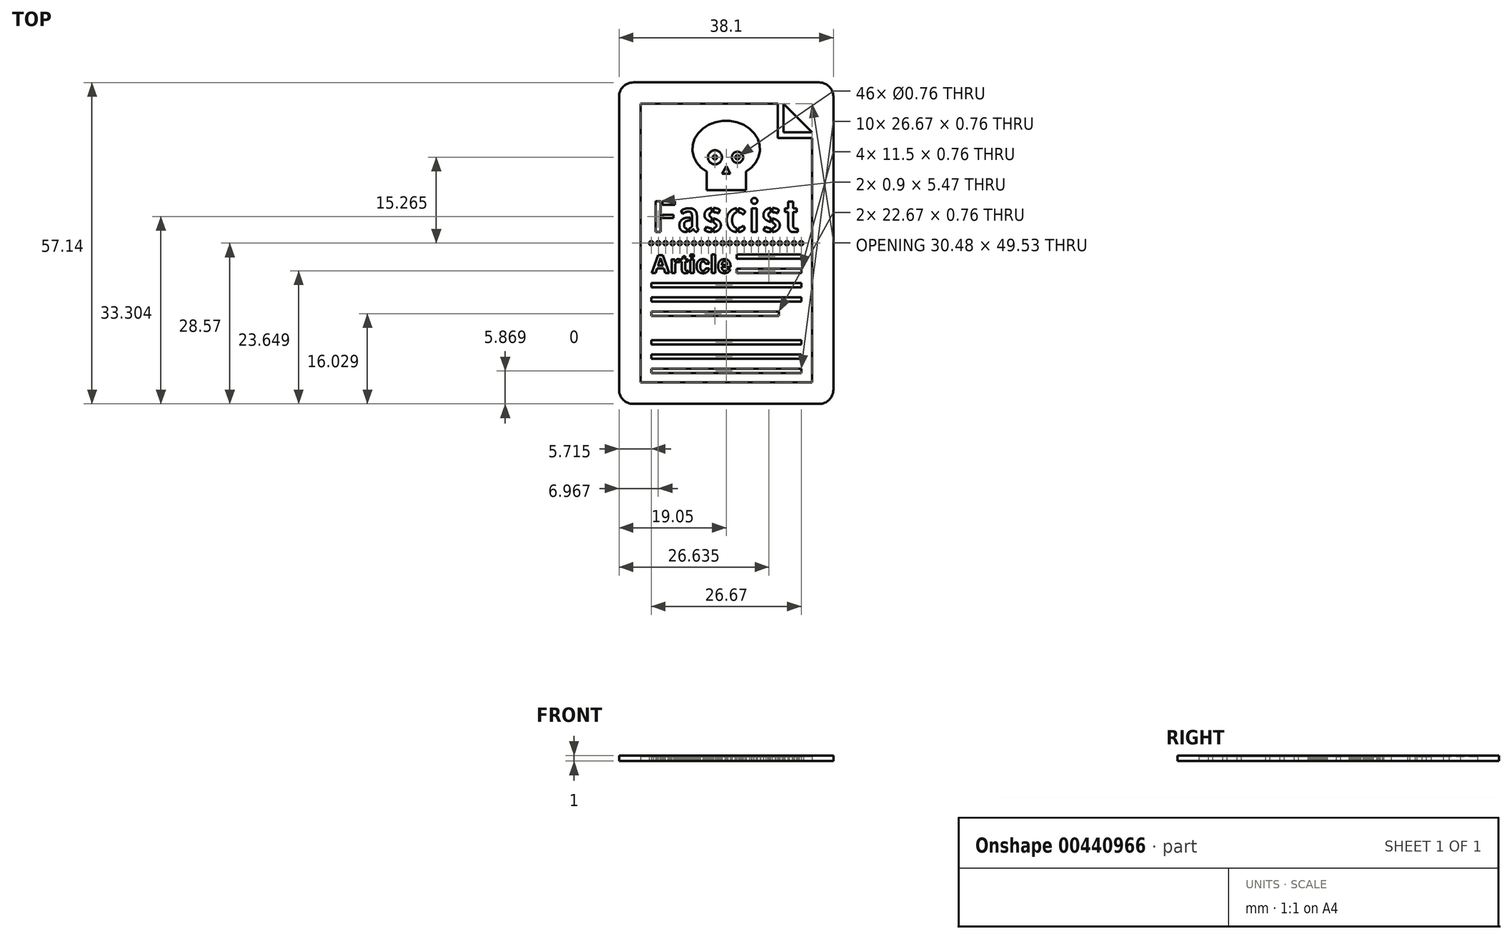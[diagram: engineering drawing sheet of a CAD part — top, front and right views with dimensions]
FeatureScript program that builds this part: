
annotation { "Feature Type Name" : "Feature", "Feature Type Description" : "" }
export const myFeature = defineFeature(function(context is Context, id is Id, definition is map)
    precondition{}
    {
        {
            var Q0;
            Q0=qCreatedBy(makeId("Top.planeOp"),FACE);
            var sketch = newSketch(context, id + "F0", { "sketchPlane" : qUnion([Q0])});
            skLineSegment(sketch, "E0.bottom", {"start": v(16.5, 28.58) * mm, "end": v(-16.51, 28.58) * mm});
            skLineSegment(sketch, "E0.top", {"start": v(16.51, -28.58) * mm, "end": v(-16.5, -28.58) * mm});
            skLineSegment(sketch, "E0.left", {"start": v(19.05, 26.04) * mm, "end": v(19.05, -26.04) * mm});
            skLineSegment(sketch, "E0.right", {"start": v(-19.05, 26.04) * mm, "end": v(-19.05, -26.04) * mm});
            skPoint(sketch, "E0.middle", {"position": v(0, 0) * mm});
            skPoint(sketch, "E1.visualSharp", {"position": v(-19.05, 28.58) * mm});
            skArc(sketch, "E1.filletArc", {"start": v(-16.51, 28.58) * mm, "mid": v(-18.3, 27.83) * mm, "end": v(-19.05, 26.04) * mm});
            skPoint(sketch, "E2.visualSharp", {"position": v(19.05, 28.58) * mm});
            skArc(sketch, "E2.filletArc", {"start": v(19.05, 26.04) * mm, "mid": v(18.3, 27.83) * mm, "end": v(16.5, 28.58) * mm});
            skPoint(sketch, "E3.visualSharp", {"position": v(19.05, -28.58) * mm});
            skArc(sketch, "E3.filletArc", {"start": v(16.51, -28.58) * mm, "mid": v(18.3, -27.83) * mm, "end": v(19.05, -26.04) * mm});
            skPoint(sketch, "E4.visualSharp", {"position": v(-19.05, -28.58) * mm});
            skArc(sketch, "E4.filletArc", {"start": v(-19.05, -26.04) * mm, "mid": v(-18.3, -27.83) * mm, "end": v(-16.5, -28.58) * mm});
            skLineSegment(sketch, "E5.bottom", {"start": v(9.14, 24.76) * mm, "end": v(-15.24, 24.76) * mm});
            skLineSegment(sketch, "E5.top", {"start": v(15.24, -24.77) * mm, "end": v(-15.24, -24.77) * mm});
            skLineSegment(sketch, "E5.left", {"start": v(15.24, 18.67) * mm, "end": v(15.24, -24.77) * mm});
            skLineSegment(sketch, "E5.right", {"start": v(-15.24, 24.77) * mm, "end": v(-15.24, -24.77) * mm});
            skLineSegment(sketch, "E6.top", {"start": v(15.24, 19.68) * mm, "end": v(10.16, 19.68) * mm});
            skLineSegment(sketch, "E6.right", {"start": v(10.16, 24.76) * mm, "end": v(10.16, 19.68) * mm});
            skLineSegment(sketch, "E7", {"start": v(10.16, 24.76) * mm, "end": v(15.24, 19.68) * mm});
            skPoint(sketch, "E8.orphan", {"position": v(15.24, 24.76) * mm});
            skLineSegment(sketch, "E9.0", {"start": v(15.24, 18.67) * mm, "end": v(9.14, 18.67) * mm});
            skLineSegment(sketch, "E9.1", {"start": v(9.14, 24.76) * mm, "end": v(9.14, 18.67) * mm});
            skEllipticalArc(sketch, "E10", {});
            skLineSegment(sketch, "E11.bottom", {"start": v(3.5, 9.4) * mm, "end": v(-3.5, 9.4) * mm});
            skLineSegment(sketch, "E11.left", {"start": v(3.5, 9.4) * mm, "end": v(3.5, 12.7) * mm});
            skLineSegment(sketch, "E11.right", {"start": v(-3.5, 9.4) * mm, "end": v(-3.5, 12.7) * mm});
            skPoint(sketch, "E11.middle", {"position": v(0, 15.06) * mm});
            skPoint(sketch, "E11.top.start.orphan", {"position": v(3.5, 20.72) * mm});
            skPoint(sketch, "E12.orphan", {"position": v(-3.5, 20.72) * mm});
            skCircle(sketch, "E13", {"center": v(-2, 15.26) * mm, "radius": 1.25 * mm});
            skLineSegment(sketch, "E14", {"start": v(0, 13.66) * mm, "end": v(-0.75, 12.37) * mm});
            skLineSegment(sketch, "E15", {"start": v(-0.75, 12.37) * mm, "end": v(0.75, 12.37) * mm});
            skLineSegment(sketch, "E16", {"start": v(0, 13.66) * mm, "end": v(0.75, 12.37) * mm});
            skCircle(sketch, "E17", {"center": v(2, 15.26) * mm, "radius": 1 * mm});
            skLineSegment(sketch, "E18.0", {"start": v(2.74, 10.17) * mm, "end": v(2.13, 10.17) * mm});
            skLineSegment(sketch, "E18.1", {"start": v(2.74, 10.17) * mm, "end": v(2.74, 13.15) * mm});
            skFitSpline(sketch, "E18.2", {"points": [v(5.17, 15.96) * mm, v(5.27, 16.76) * mm, v(5.17, 17.57) * mm, v(4.9, 18.34) * mm, v(4.42, 19.08) * mm, v(3.78, 19.73) * mm, v(2.99, 20.28) * mm, v(2.06, 20.7) * mm, v(1.06, 20.94) * mm, v(0, 21.03) * mm, v(-1.06, 20.94) * mm, v(-2.06, 20.7) * mm, v(-2.99, 20.28) * mm, v(-3.78, 19.73) * mm, v(-4.42, 19.08) * mm, v(-4.9, 18.34) * mm, v(-5.17, 17.57) * mm, v(-5.27, 16.76) * mm, v(-5.17, 15.96) * mm, v(-4.9, 15.19) * mm, v(-4.42, 14.45) * mm, v(-3.78, 13.8) * mm, v(-2.99, 13.25) * mm, v(-2.06, 12.84) * mm, v(-1.06, 12.59) * mm, v(0, 12.5) * mm, v(1.06, 12.59) * mm, v(2.06, 12.84) * mm, v(2.99, 13.25) * mm, v(3.78, 13.8) * mm, v(4.42, 14.45) * mm, v(4.9, 15.19) * mm, v(5.17, 15.96) * mm, v(5.27, 16.76) * mm, v(5.17, 17.57) * mm]});
            skLineSegment(sketch, "E18.3", {"start": v(-2.74, 10.17) * mm, "end": v(-2.74, 13.15) * mm});
            skLineSegment(sketch, "E19.top", {"start": v(-2.13, 11.17) * mm, "end": v(-1.78, 11.17) * mm});
            skLineSegment(sketch, "E19.left", {"start": v(-2.13, 10.17) * mm, "end": v(-2.13, 11.17) * mm});
            skLineSegment(sketch, "E19.right", {"start": v(-1.78, 10.17) * mm, "end": v(-1.78, 11.17) * mm});
            skLineSegment(sketch, "E20.trimOffspring", {"start": v(-2.13, 10.17) * mm, "end": v(-2.74, 10.17) * mm});
            skLineSegment(sketch, "E21.top", {"start": v(-0.83, 11.17) * mm, "end": v(-0.48, 11.17) * mm});
            skLineSegment(sketch, "E21.left", {"start": v(-0.83, 10.17) * mm, "end": v(-0.83, 11.17) * mm});
            skLineSegment(sketch, "E21.right", {"start": v(-0.48, 10.17) * mm, "end": v(-0.48, 11.17) * mm});
            skLineSegment(sketch, "E22.top", {"start": v(0.48, 11.17) * mm, "end": v(0.83, 11.17) * mm});
            skLineSegment(sketch, "E22.left", {"start": v(0.48, 10.17) * mm, "end": v(0.48, 11.17) * mm});
            skLineSegment(sketch, "E22.right", {"start": v(0.83, 10.17) * mm, "end": v(0.83, 11.17) * mm});
            skLineSegment(sketch, "E23.top", {"start": v(1.78, 11.17) * mm, "end": v(2.13, 11.17) * mm});
            skLineSegment(sketch, "E23.left", {"start": v(1.78, 10.17) * mm, "end": v(1.78, 11.17) * mm});
            skLineSegment(sketch, "E23.right", {"start": v(2.13, 10.17) * mm, "end": v(2.13, 11.17) * mm});
            skLineSegment(sketch, "E24.trimOffspring", {"start": v(-0.83, 10.17) * mm, "end": v(-1.78, 10.17) * mm});
            skLineSegment(sketch, "E25.trimOffspring", {"start": v(0.48, 10.17) * mm, "end": v(-0.48, 10.17) * mm});
            skLineSegment(sketch, "E26.trimOffspring", {"start": v(1.78, 10.17) * mm, "end": v(0.83, 10.17) * mm});
            skText(sketch, "E27", { "text": "Fascist", "fontName": "AllertaStencil-Regular.ttf"});
            skCircle(sketch, "E28", {"center": v(-13.34, 0) * mm, "radius": 0.38 * mm});
            skPoint(sketch, "E28.centerSnap0", {"position": v(-15.24, 0) * mm});
            skCircle(sketch, "E29.1.0.0", {"center": v(-12.07, 0) * mm, "radius": 0.38 * mm});
            skCircle(sketch, "E29.2.0.0", {"center": v(-10.8, 0) * mm, "radius": 0.38 * mm});
            skCircle(sketch, "E29.3.0.0", {"center": v(-9.53, 0) * mm, "radius": 0.38 * mm});
            skCircle(sketch, "E29.4.0.0", {"center": v(-8.26, 0) * mm, "radius": 0.38 * mm});
            skCircle(sketch, "E29.5.0.0", {"center": v(-6.99, 0) * mm, "radius": 0.38 * mm});
            skCircle(sketch, "E29.6.0.0", {"center": v(-5.72, 0) * mm, "radius": 0.38 * mm});
            skCircle(sketch, "E29.7.0.0", {"center": v(-4.45, 0) * mm, "radius": 0.38 * mm});
            skCircle(sketch, "E29.8.0.0", {"center": v(-3.18, 0) * mm, "radius": 0.38 * mm});
            skCircle(sketch, "E29.9.0.0", {"center": v(-1.9, 0) * mm, "radius": 0.38 * mm});
            skCircle(sketch, "E29.10.0.0", {"center": v(-0.64, 0) * mm, "radius": 0.38 * mm});
            skCircle(sketch, "E29.11.0.0", {"center": v(0.63, 0) * mm, "radius": 0.38 * mm});
            skCircle(sketch, "E29.12.0.0", {"center": v(1.9, 0) * mm, "radius": 0.38 * mm});
            skCircle(sketch, "E29.13.0.0", {"center": v(3.17, 0) * mm, "radius": 0.38 * mm});
            skCircle(sketch, "E29.14.0.0", {"center": v(4.44, 0) * mm, "radius": 0.38 * mm});
            skCircle(sketch, "E29.15.0.0", {"center": v(5.71, 0) * mm, "radius": 0.38 * mm});
            skCircle(sketch, "E29.16.0.0", {"center": v(6.99, 0) * mm, "radius": 0.38 * mm});
            skCircle(sketch, "E29.17.0.0", {"center": v(8.26, 0) * mm, "radius": 0.38 * mm});
            skCircle(sketch, "E29.18.0.0", {"center": v(9.53, 0) * mm, "radius": 0.38 * mm});
            skCircle(sketch, "E29.19.0.0", {"center": v(10.8, 0) * mm, "radius": 0.38 * mm});
            skCircle(sketch, "E29.20.0.0", {"center": v(12.07, 0) * mm, "radius": 0.38 * mm});
            skCircle(sketch, "E29.21.0.0", {"center": v(13.34, 0) * mm, "radius": 0.38 * mm});
            skLineSegment(sketch, "E29.direction1", {"start": v(-13.34, 0) * mm, "end": v(-12.07, 0) * mm, "construction": true});
            skText(sketch, "E30", { "text": "Article", "fontName": "Arimo-Bold.ttf"});
            skLineSegment(sketch, "E31.bottom", {"start": v(1.84, -2) * mm, "end": v(13.34, -2) * mm});
            skLineSegment(sketch, "E31.top", {"start": v(1.84, -2.76) * mm, "end": v(13.34, -2.76) * mm});
            skLineSegment(sketch, "E31.left", {"start": v(1.84, -2) * mm, "end": v(1.84, -2.76) * mm});
            skLineSegment(sketch, "E31.right", {"start": v(13.34, -2) * mm, "end": v(13.34, -2.76) * mm});
            skLineSegment(sketch, "E32.bottom", {"start": v(1.84, -4.54) * mm, "end": v(13.34, -4.54) * mm});
            skLineSegment(sketch, "E32.top", {"start": v(1.84, -5.3) * mm, "end": v(13.34, -5.3) * mm});
            skLineSegment(sketch, "E32.left", {"start": v(1.84, -4.54) * mm, "end": v(1.84, -5.3) * mm});
            skLineSegment(sketch, "E32.right", {"start": v(13.34, -4.54) * mm, "end": v(13.34, -5.3) * mm});
            skLineSegment(sketch, "E33.bottom", {"start": v(-13.34, -7.08) * mm, "end": v(13.34, -7.08) * mm});
            skLineSegment(sketch, "E33.top", {"start": v(-13.34, -7.84) * mm, "end": v(13.34, -7.84) * mm});
            skLineSegment(sketch, "E33.left", {"start": v(-13.34, -7.08) * mm, "end": v(-13.34, -7.84) * mm});
            skLineSegment(sketch, "E33.right", {"start": v(13.34, -7.08) * mm, "end": v(13.34, -7.84) * mm});
            skLineSegment(sketch, "E34.bottom", {"start": v(-13.34, -9.62) * mm, "end": v(13.34, -9.62) * mm});
            skLineSegment(sketch, "E34.top", {"start": v(-13.34, -10.38) * mm, "end": v(13.34, -10.38) * mm});
            skLineSegment(sketch, "E34.left", {"start": v(-13.34, -9.62) * mm, "end": v(-13.34, -10.38) * mm});
            skLineSegment(sketch, "E34.right", {"start": v(13.34, -9.62) * mm, "end": v(13.34, -10.38) * mm});
            skLineSegment(sketch, "E35.bottom", {"start": v(-13.34, -12.16) * mm, "end": v(9.33, -12.16) * mm});
            skLineSegment(sketch, "E35.top", {"start": v(-13.34, -12.92) * mm, "end": v(9.33, -12.92) * mm});
            skLineSegment(sketch, "E35.left", {"start": v(-13.34, -12.16) * mm, "end": v(-13.34, -12.92) * mm});
            skLineSegment(sketch, "E35.right", {"start": v(9.33, -12.16) * mm, "end": v(9.33, -12.92) * mm});
            skLineSegment(sketch, "E36.bottom", {"start": v(-13.34, -19.78) * mm, "end": v(13.33, -19.78) * mm});
            skLineSegment(sketch, "E36.top", {"start": v(-13.34, -20.54) * mm, "end": v(13.33, -20.54) * mm});
            skLineSegment(sketch, "E36.left", {"start": v(-13.34, -19.78) * mm, "end": v(-13.34, -20.54) * mm});
            skLineSegment(sketch, "E36.right", {"start": v(13.34, -19.78) * mm, "end": v(13.34, -20.54) * mm});
            skLineSegment(sketch, "E37.bottom", {"start": v(-13.34, -22.32) * mm, "end": v(13.34, -22.32) * mm});
            skLineSegment(sketch, "E37.top", {"start": v(-13.34, -23.08) * mm, "end": v(13.34, -23.08) * mm});
            skLineSegment(sketch, "E37.left", {"start": v(-13.34, -22.32) * mm, "end": v(-13.34, -23.08) * mm});
            skLineSegment(sketch, "E37.right", {"start": v(13.34, -22.32) * mm, "end": v(13.34, -23.08) * mm});
            skLineSegment(sketch, "E38.bottom", {"start": v(-13.34, -17.24) * mm, "end": v(13.34, -17.24) * mm});
            skLineSegment(sketch, "E38.top", {"start": v(-13.34, -18) * mm, "end": v(13.34, -18) * mm});
            skLineSegment(sketch, "E38.left", {"start": v(-13.34, -17.24) * mm, "end": v(-13.34, -18) * mm});
            skLineSegment(sketch, "E38.right", {"start": v(13.34, -17.24) * mm, "end": v(13.34, -18) * mm});
            skCircle(sketch, "E39", {"center": v(-2, 15.26) * mm, "radius": 0.38 * mm});
            skCircle(sketch, "E40", {"center": v(2, 15.26) * mm, "radius": 0.38 * mm});
            const initialGuessF0  = {"E10": [0, 0.016765, 1, 0, 0.006, 0.005, 5.335215565796689, 4.089562394972688], "E27": [-0.01324, 0.002, 1, 0, 0.00547], "E30": [-0.01334, -0.0053, 1, 0, 0.0033]};
            skSetInitialGuess(sketch, initialGuessF0);
            skSolve(sketch);
        }
        {
            var Q0;
            Q0 = qSketchRegion(id + "F0", true);
            var Q1;
            Q1=makeQuery(id+"F0.imprint","IMPRINT",FACE,{"disambiguationData":[TD([[makeQuery(id+"F0.imprint","IMPRINT",EDGE,{"derivedFrom":sQuery(id+"F0.wireOp",EDGE,"E10")}),1.0]])]});
            var Q2;
            Q2=makeQuery(id+"F0.imprint","IMPRINT",FACE,{"disambiguationData":[TD([[makeQuery(id+"F0.imprint","IMPRINT",EDGE,{"derivedFrom":sQuery(id+"F0.wireOp",EDGE,"E17")}),1.0]])]});
            var Q3;
            Q3=makeQuery(id+"F0.imprint","IMPRINT",FACE,{"disambiguationData":[TD([[makeQuery(id+"F0.imprint","IMPRINT",EDGE,{"derivedFrom":sQuery(id+"F0.wireOp",EDGE,"E13")}),1.0]])]});
            var Q4;
            Q4=makeQuery(id+"F0.imprint","IMPRINT",FACE,{"disambiguationData":[TD([[makeQuery(id+"F0.imprint","IMPRINT",EDGE,{"derivedFrom":sQuery(id+"F0.wireOp",EDGE,"E14")}),1.0]])]});
            var Q5;
            Q5=makeQuery(id+"F0.imprint","IMPRINT",FACE,{"disambiguationData":[TD([[makeQuery(id+"F0.imprint","IMPRINT",EDGE,{"derivedFrom":sQuery(id+"F0.wireOp",EDGE,"E27.sketch_text.stroke-0")}),-1.0]])]});
            var Q6;
            Q6=makeQuery(id+"F0.imprint","IMPRINT",FACE,{"disambiguationData":[TD([[makeQuery(id+"F0.imprint","IMPRINT",EDGE,{"derivedFrom":sQuery(id+"F0.wireOp",EDGE,"E27.sketch_text.stroke-8")}),-1.0]])]});
            var Q7;
            Q7=makeQuery(id+"F0.imprint","IMPRINT",FACE,{"disambiguationData":[TD([[makeQuery(id+"F0.imprint","IMPRINT",EDGE,{"derivedFrom":sQuery(id+"F0.wireOp",EDGE,"E27.sketch_text.stroke-4")}),-1.0]])]});
            var Q8;
            Q8=makeQuery(id+"F0.imprint","IMPRINT",FACE,{"disambiguationData":[TD([[makeQuery(id+"F0.imprint","IMPRINT",EDGE,{"derivedFrom":sQuery(id+"F0.wireOp",EDGE,"E27.sketch_text.stroke-31")}),-1.0]])]});
            var Q9;
            Q9=makeQuery(id+"F0.imprint","IMPRINT",FACE,{"disambiguationData":[TD([[makeQuery(id+"F0.imprint","IMPRINT",EDGE,{"derivedFrom":sQuery(id+"F0.wireOp",EDGE,"E27.sketch_text.stroke-12")}),-1.0]])]});
            var Q10;
            Q10=makeQuery(id+"F0.imprint","IMPRINT",FACE,{"disambiguationData":[TD([[makeQuery(id+"F0.imprint","IMPRINT",EDGE,{"derivedFrom":sQuery(id+"F0.wireOp",EDGE,"E27.sketch_text.stroke-96")}),-1.0]])]});
            var Q11;
            Q11=makeQuery(id+"F0.imprint","IMPRINT",FACE,{"disambiguationData":[TD([[makeQuery(id+"F0.imprint","IMPRINT",EDGE,{"derivedFrom":sQuery(id+"F0.wireOp",EDGE,"E27.sketch_text.stroke-87")}),-1.0]])]});
            var Q12;
            Q12=makeQuery(id+"F0.imprint","IMPRINT",FACE,{"disambiguationData":[TD([[makeQuery(id+"F0.imprint","IMPRINT",EDGE,{"derivedFrom":sQuery(id+"F0.wireOp",EDGE,"E27.sketch_text.stroke-67")}),-1.0]])]});
            var Q13;
            Q13=makeQuery(id+"F0.imprint","IMPRINT",FACE,{"disambiguationData":[TD([[makeQuery(id+"F0.imprint","IMPRINT",EDGE,{"derivedFrom":sQuery(id+"F0.wireOp",EDGE,"E27.sketch_text.stroke-81")}),-1.0]])]});
            var Q14;
            Q14=makeQuery(id+"F0.imprint","IMPRINT",FACE,{"disambiguationData":[TD([[makeQuery(id+"F0.imprint","IMPRINT",EDGE,{"derivedFrom":sQuery(id+"F0.wireOp",EDGE,"E27.sketch_text.stroke-116")}),-1.0]])]});
            var Q15;
            Q15=makeQuery(id+"F0.imprint","IMPRINT",FACE,{"disambiguationData":[TD([[makeQuery(id+"F0.imprint","IMPRINT",EDGE,{"derivedFrom":sQuery(id+"F0.wireOp",EDGE,"E27.sketch_text.stroke-122")}),-1.0]])]});
            var Q16;
            Q16=makeQuery(id+"F0.imprint","IMPRINT",FACE,{"disambiguationData":[TD([[makeQuery(id+"F0.imprint","IMPRINT",EDGE,{"derivedFrom":sQuery(id+"F0.wireOp",EDGE,"E27.sketch_text.stroke-110")}),-1.0]])]});
            var Q17;
            Q17=makeQuery(id+"F0.imprint","IMPRINT",FACE,{"disambiguationData":[TD([[makeQuery(id+"F0.imprint","IMPRINT",EDGE,{"derivedFrom":sQuery(id+"F0.wireOp",EDGE,"E27.sketch_text.stroke-142")}),-1.0]])]});
            var Q18;
            Q18=makeQuery(id+"F0.imprint","IMPRINT",FACE,{"disambiguationData":[TD([[makeQuery(id+"F0.imprint","IMPRINT",EDGE,{"derivedFrom":sQuery(id+"F0.wireOp",EDGE,"E27.sketch_text.stroke-138")}),-1.0]])]});
            var Q19;
            Q19=makeQuery(id+"F0.imprint","IMPRINT",FACE,{"disambiguationData":[TD([[makeQuery(id+"F0.imprint","IMPRINT",EDGE,{"derivedFrom":sQuery(id+"F0.wireOp",EDGE,"E27.sketch_text.stroke-170")}),-1.0]])]});
            var Q20;
            Q20=makeQuery(id+"F0.imprint","IMPRINT",FACE,{"disambiguationData":[TD([[makeQuery(id+"F0.imprint","IMPRINT",EDGE,{"derivedFrom":sQuery(id+"F0.wireOp",EDGE,"E27.sketch_text.stroke-179")}),-1.0]])]});
            var Q21;
            Q21=makeQuery(id+"F0.imprint","IMPRINT",FACE,{"disambiguationData":[TD([[makeQuery(id+"F0.imprint","IMPRINT",EDGE,{"derivedFrom":sQuery(id+"F0.wireOp",EDGE,"E27.sketch_text.stroke-150")}),-1.0]])]});
            var Q22;
            Q22=makeQuery(id+"F0.imprint","IMPRINT",FACE,{"disambiguationData":[TD([[makeQuery(id+"F0.imprint","IMPRINT",EDGE,{"derivedFrom":sQuery(id+"F0.wireOp",EDGE,"E27.sketch_text.stroke-164")}),-1.0]])]});
            var Q23;
            Q23=makeQuery(id+"F0.imprint","IMPRINT",FACE,{"disambiguationData":[TD([[makeQuery(id+"F0.imprint","IMPRINT",EDGE,{"derivedFrom":sQuery(id+"F0.wireOp",EDGE,"E27.sketch_text.stroke-193")}),-1.0]])]});
            var Q24;
            Q24=makeQuery(id+"F0.imprint","IMPRINT",FACE,{"disambiguationData":[TD([[makeQuery(id+"F0.imprint","IMPRINT",EDGE,{"derivedFrom":sQuery(id+"F0.wireOp",EDGE,"E28")}),1.0]])]});
            var Q25;
            Q25=makeQuery(id+"F0.imprint","IMPRINT",FACE,{"disambiguationData":[TD([[makeQuery(id+"F0.imprint","IMPRINT",EDGE,{"derivedFrom":sQuery(id+"F0.wireOp",EDGE,"E29.1.0.0")}),1.0]])]});
            var Q26;
            Q26=makeQuery(id+"F0.imprint","IMPRINT",FACE,{"disambiguationData":[TD([[makeQuery(id+"F0.imprint","IMPRINT",EDGE,{"derivedFrom":sQuery(id+"F0.wireOp",EDGE,"E29.2.0.0")}),1.0]])]});
            var Q27;
            Q27=makeQuery(id+"F0.imprint","IMPRINT",FACE,{"disambiguationData":[TD([[makeQuery(id+"F0.imprint","IMPRINT",EDGE,{"derivedFrom":sQuery(id+"F0.wireOp",EDGE,"E29.3.0.0")}),1.0]])]});
            var Q28;
            Q28=makeQuery(id+"F0.imprint","IMPRINT",FACE,{"disambiguationData":[TD([[makeQuery(id+"F0.imprint","IMPRINT",EDGE,{"derivedFrom":sQuery(id+"F0.wireOp",EDGE,"E29.4.0.0")}),1.0]])]});
            var Q29;
            Q29=makeQuery(id+"F0.imprint","IMPRINT",FACE,{"disambiguationData":[TD([[makeQuery(id+"F0.imprint","IMPRINT",EDGE,{"derivedFrom":sQuery(id+"F0.wireOp",EDGE,"E29.5.0.0")}),1.0]])]});
            var Q30;
            Q30=makeQuery(id+"F0.imprint","IMPRINT",FACE,{"disambiguationData":[TD([[makeQuery(id+"F0.imprint","IMPRINT",EDGE,{"derivedFrom":sQuery(id+"F0.wireOp",EDGE,"E29.6.0.0")}),1.0]])]});
            var Q31;
            Q31=makeQuery(id+"F0.imprint","IMPRINT",FACE,{"disambiguationData":[TD([[makeQuery(id+"F0.imprint","IMPRINT",EDGE,{"derivedFrom":sQuery(id+"F0.wireOp",EDGE,"E29.7.0.0")}),1.0]])]});
            var Q32;
            Q32=makeQuery(id+"F0.imprint","IMPRINT",FACE,{"disambiguationData":[TD([[makeQuery(id+"F0.imprint","IMPRINT",EDGE,{"derivedFrom":sQuery(id+"F0.wireOp",EDGE,"E29.8.0.0")}),1.0]])]});
            var Q33;
            Q33=makeQuery(id+"F0.imprint","IMPRINT",FACE,{"disambiguationData":[TD([[makeQuery(id+"F0.imprint","IMPRINT",EDGE,{"derivedFrom":sQuery(id+"F0.wireOp",EDGE,"E29.9.0.0")}),1.0]])]});
            var Q34;
            Q34=makeQuery(id+"F0.imprint","IMPRINT",FACE,{"disambiguationData":[TD([[makeQuery(id+"F0.imprint","IMPRINT",EDGE,{"derivedFrom":sQuery(id+"F0.wireOp",EDGE,"E29.10.0.0")}),1.0]])]});
            var Q35;
            Q35=makeQuery(id+"F0.imprint","IMPRINT",FACE,{"disambiguationData":[TD([[makeQuery(id+"F0.imprint","IMPRINT",EDGE,{"derivedFrom":sQuery(id+"F0.wireOp",EDGE,"E29.11.0.0")}),1.0]])]});
            var Q36;
            Q36=makeQuery(id+"F0.imprint","IMPRINT",FACE,{"disambiguationData":[TD([[makeQuery(id+"F0.imprint","IMPRINT",EDGE,{"derivedFrom":sQuery(id+"F0.wireOp",EDGE,"E29.12.0.0")}),1.0]])]});
            var Q37;
            Q37=makeQuery(id+"F0.imprint","IMPRINT",FACE,{"disambiguationData":[TD([[makeQuery(id+"F0.imprint","IMPRINT",EDGE,{"derivedFrom":sQuery(id+"F0.wireOp",EDGE,"E29.13.0.0")}),1.0]])]});
            var Q38;
            Q38=makeQuery(id+"F0.imprint","IMPRINT",FACE,{"disambiguationData":[TD([[makeQuery(id+"F0.imprint","IMPRINT",EDGE,{"derivedFrom":sQuery(id+"F0.wireOp",EDGE,"E29.14.0.0")}),1.0]])]});
            var Q39;
            Q39=makeQuery(id+"F0.imprint","IMPRINT",FACE,{"disambiguationData":[TD([[makeQuery(id+"F0.imprint","IMPRINT",EDGE,{"derivedFrom":sQuery(id+"F0.wireOp",EDGE,"E29.15.0.0")}),1.0]])]});
            var Q40;
            Q40=makeQuery(id+"F0.imprint","IMPRINT",FACE,{"disambiguationData":[TD([[makeQuery(id+"F0.imprint","IMPRINT",EDGE,{"derivedFrom":sQuery(id+"F0.wireOp",EDGE,"E29.16.0.0")}),1.0]])]});
            var Q41;
            Q41=makeQuery(id+"F0.imprint","IMPRINT",FACE,{"disambiguationData":[TD([[makeQuery(id+"F0.imprint","IMPRINT",EDGE,{"derivedFrom":sQuery(id+"F0.wireOp",EDGE,"E29.17.0.0")}),1.0]])]});
            var Q42;
            Q42=makeQuery(id+"F0.imprint","IMPRINT",FACE,{"disambiguationData":[TD([[makeQuery(id+"F0.imprint","IMPRINT",EDGE,{"derivedFrom":sQuery(id+"F0.wireOp",EDGE,"E29.18.0.0")}),1.0]])]});
            var Q43;
            Q43=makeQuery(id+"F0.imprint","IMPRINT",FACE,{"disambiguationData":[TD([[makeQuery(id+"F0.imprint","IMPRINT",EDGE,{"derivedFrom":sQuery(id+"F0.wireOp",EDGE,"E29.19.0.0")}),1.0]])]});
            var Q44;
            Q44=makeQuery(id+"F0.imprint","IMPRINT",FACE,{"disambiguationData":[TD([[makeQuery(id+"F0.imprint","IMPRINT",EDGE,{"derivedFrom":sQuery(id+"F0.wireOp",EDGE,"E29.20.0.0")}),1.0]])]});
            var Q45;
            Q45=makeQuery(id+"F0.imprint","IMPRINT",FACE,{"disambiguationData":[TD([[makeQuery(id+"F0.imprint","IMPRINT",EDGE,{"derivedFrom":sQuery(id+"F0.wireOp",EDGE,"E29.21.0.0")}),1.0]])]});
            var Q46;
            Q46=makeQuery(id+"F0.imprint","IMPRINT",FACE,{"disambiguationData":[TD([[makeQuery(id+"F0.imprint","IMPRINT",EDGE,{"derivedFrom":sQuery(id+"F0.wireOp",EDGE,"E30.sketch_text.stroke-0")}),-1.0]])]});
            var Q47;
            Q47=makeQuery(id+"F0.imprint","IMPRINT",FACE,{"disambiguationData":[TD([[makeQuery(id+"F0.imprint","IMPRINT",EDGE,{"derivedFrom":sQuery(id+"F0.wireOp",EDGE,"E30.sketch_text.stroke-15")}),-1.0]])]});
            var Q48;
            Q48=makeQuery(id+"F0.imprint","IMPRINT",FACE,{"disambiguationData":[TD([[makeQuery(id+"F0.imprint","IMPRINT",EDGE,{"derivedFrom":sQuery(id+"F0.wireOp",EDGE,"E30.sketch_text.stroke-32")}),-1.0]])]});
            var Q49;
            Q49=makeQuery(id+"F0.imprint","IMPRINT",FACE,{"disambiguationData":[TD([[makeQuery(id+"F0.imprint","IMPRINT",EDGE,{"derivedFrom":sQuery(id+"F0.wireOp",EDGE,"E30.sketch_text.stroke-54")}),-1.0]])]});
            var Q50;
            Q50=makeQuery(id+"F0.imprint","IMPRINT",FACE,{"disambiguationData":[TD([[makeQuery(id+"F0.imprint","IMPRINT",EDGE,{"derivedFrom":sQuery(id+"F0.wireOp",EDGE,"E30.sketch_text.stroke-50")}),-1.0]])]});
            var Q51;
            Q51=makeQuery(id+"F0.imprint","IMPRINT",FACE,{"disambiguationData":[TD([[makeQuery(id+"F0.imprint","IMPRINT",EDGE,{"derivedFrom":sQuery(id+"F0.wireOp",EDGE,"E30.sketch_text.stroke-58")}),-1.0]])]});
            var Q52;
            Q52=makeQuery(id+"F0.imprint","IMPRINT",FACE,{"disambiguationData":[TD([[makeQuery(id+"F0.imprint","IMPRINT",EDGE,{"derivedFrom":sQuery(id+"F0.wireOp",EDGE,"E30.sketch_text.stroke-75")}),-1.0]])]});
            var Q53;
            Q53=makeQuery(id+"F0.imprint","IMPRINT",FACE,{"disambiguationData":[TD([[makeQuery(id+"F0.imprint","IMPRINT",EDGE,{"derivedFrom":sQuery(id+"F0.wireOp",EDGE,"E30.sketch_text.stroke-79")}),-1.0]])]});
            var Q54;
            Q54=makeQuery(id+"F0.imprint","IMPRINT",FACE,{"disambiguationData":[TD([[makeQuery(id+"F0.imprint","IMPRINT",EDGE,{"derivedFrom":sQuery(id+"F0.wireOp",EDGE,"E31.bottom")}),-1.0]])]});
            var Q55;
            Q55=makeQuery(id+"F0.imprint","IMPRINT",FACE,{"disambiguationData":[TD([[makeQuery(id+"F0.imprint","IMPRINT",EDGE,{"derivedFrom":sQuery(id+"F0.wireOp",EDGE,"E32.bottom")}),-1.0]])]});
            var Q56;
            Q56=makeQuery(id+"F0.imprint","IMPRINT",FACE,{"disambiguationData":[TD([[makeQuery(id+"F0.imprint","IMPRINT",EDGE,{"derivedFrom":sQuery(id+"F0.wireOp",EDGE,"E33.bottom")}),-1.0]])]});
            var Q57;
            Q57=makeQuery(id+"F0.imprint","IMPRINT",FACE,{"disambiguationData":[TD([[makeQuery(id+"F0.imprint","IMPRINT",EDGE,{"derivedFrom":sQuery(id+"F0.wireOp",EDGE,"E34.bottom")}),-1.0]])]});
            var Q58;
            Q58=makeQuery(id+"F0.imprint","IMPRINT",FACE,{"disambiguationData":[TD([[makeQuery(id+"F0.imprint","IMPRINT",EDGE,{"derivedFrom":sQuery(id+"F0.wireOp",EDGE,"E35.bottom")}),-1.0]])]});
            var Q59;
            Q59=makeQuery(id+"F0.imprint","IMPRINT",FACE,{"disambiguationData":[TD([[makeQuery(id+"F0.imprint","IMPRINT",EDGE,{"derivedFrom":sQuery(id+"F0.wireOp",EDGE,"E38.bottom")}),-1.0]])]});
            var Q60;
            Q60=makeQuery(id+"F0.imprint","IMPRINT",FACE,{"disambiguationData":[TD([[makeQuery(id+"F0.imprint","IMPRINT",EDGE,{"derivedFrom":sQuery(id+"F0.wireOp",EDGE,"E36.bottom")}),-1.0]])]});
            var Q61;
            Q61=makeQuery(id+"F0.imprint","IMPRINT",FACE,{"disambiguationData":[TD([[makeQuery(id+"F0.imprint","IMPRINT",EDGE,{"derivedFrom":sQuery(id+"F0.wireOp",EDGE,"E37.bottom")}),-1.0]])]});
            extrude(context, id + "F1", {"entities" : qUnion([Q0, Q1, Q2, Q3, Q4, Q5, Q6, Q7, Q8, Q9, Q10, Q11, Q12, Q13, Q14, Q15, Q16, Q17, Q18, Q19, Q20, Q21, Q22, Q23, Q24, Q25, Q26, Q27, Q28, Q29, Q30, Q31, Q32, Q33, Q34, Q35, Q36, Q37, Q38, Q39, Q40, Q41, Q42, Q43, Q44, Q45, Q46, Q47, Q48, Q49, Q50, Q51, Q52, Q53, Q54, Q55, Q56, Q57, Q58, Q59, Q60, Q61]), "depth" : 1 * mm});
        }
        {
            var Q0;
            Q0=makeQuery(id+"F0.imprint","IMPRINT",FACE,{"disambiguationData":[TD([[makeQuery(id+"F0.imprint","IMPRINT",EDGE,{"derivedFrom":sQuery(id+"F0.wireOp",EDGE,"E13")}),-1.0]])]});
            var Q1;
            Q1=makeQuery(id+"F0.imprint","IMPRINT",FACE,{"disambiguationData":[TD([[makeQuery(id+"F0.imprint","IMPRINT",EDGE,{"derivedFrom":sQuery(id+"F0.wireOp",EDGE,"E6.top")}),-1.0]])]});
            var Q2;
            Q2=makeQuery(id+"F0.imprint","IMPRINT",FACE,{"disambiguationData":[TD([[makeQuery(id+"F0.imprint","IMPRINT",EDGE,{"derivedFrom":sQuery(id+"F0.wireOp",EDGE,"E5.bottom")}),1.0]])]});
            var Q3;
            Q3=makeQuery(id+"F0.imprint","IMPRINT",FACE,{"disambiguationData":[TD([[makeQuery(id+"F0.imprint","IMPRINT",EDGE,{"derivedFrom":sQuery(id+"F0.wireOp",EDGE,"E30.sketch_text.stroke-8")}),1.0]])]});
            var Q4;
            Q4=makeQuery(id+"F0.imprint","IMPRINT",FACE,{"disambiguationData":[TD([[makeQuery(id+"F0.imprint","IMPRINT",EDGE,{"derivedFrom":sQuery(id+"F0.wireOp",EDGE,"E30.sketch_text.stroke-92")}),1.0]])]});
            var Q5;
            Q5=makeQuery(id+"F0.imprint","IMPRINT",FACE,{"disambiguationData":[TD([[makeQuery(id+"F0.imprint","IMPRINT",EDGE,{"derivedFrom":sQuery(id+"F0.wireOp",EDGE,"E39")}),1.0]])]});
            var Q6;
            Q6=makeQuery(id+"F0.imprint","IMPRINT",FACE,{"disambiguationData":[TD([[makeQuery(id+"F0.imprint","IMPRINT",EDGE,{"derivedFrom":sQuery(id+"F0.wireOp",EDGE,"E17")}),1.0]])]});
            var Q7;
            Q7=makeQuery(id+"F0.imprint","IMPRINT",FACE,{"disambiguationData":[TD([[makeQuery(id+"F0.imprint","IMPRINT",EDGE,{"derivedFrom":sQuery(id+"F0.wireOp",EDGE,"E40")}),1.0]])]});
            extrude(context, id + "F2", {"entities" : qUnion([Q0, Q1, Q2, Q3, Q4, Q5, Q6, Q7]), "depth" : .8 * mm});
        }
        {
            var Q0;
            Q0=makeQuery(id+"F0.imprint","IMPRINT",FACE,{"disambiguationData":[TD([[makeQuery(id+"F0.imprint","IMPRINT",EDGE,{"derivedFrom":sQuery(id+"F0.wireOp",EDGE,"E5.bottom")}),1.0]])]});
            var Q1;
            Q1=makeQuery(id+"F0.imprint","IMPRINT",FACE,{"disambiguationData":[TD([[makeQuery(id+"F0.imprint","IMPRINT",EDGE,{"derivedFrom":sQuery(id+"F0.wireOp",EDGE,"E13")}),-1.0]])]});
            var Q2;
            Q2=makeQuery(id+"F0.imprint","IMPRINT",FACE,{"disambiguationData":[TD([[makeQuery(id+"F0.imprint","IMPRINT",EDGE,{"derivedFrom":sQuery(id+"F0.wireOp",EDGE,"E6.top")}),-1.0]])]});
            var Q3;
            Q3=makeQuery(id+"F0.imprint","IMPRINT",FACE,{"disambiguationData":[TD([[makeQuery(id+"F0.imprint","IMPRINT",EDGE,{"derivedFrom":sQuery(id+"F0.wireOp",EDGE,"E30.sketch_text.stroke-8")}),1.0]])]});
            var Q4;
            Q4=makeQuery(id+"F0.imprint","IMPRINT",FACE,{"disambiguationData":[TD([[makeQuery(id+"F0.imprint","IMPRINT",EDGE,{"derivedFrom":sQuery(id+"F0.wireOp",EDGE,"E30.sketch_text.stroke-92")}),1.0]])]});
            var Q5;
            Q5=makeQuery(id+"F0.imprint","IMPRINT",FACE,{"disambiguationData":[TD([[makeQuery(id+"F0.imprint","IMPRINT",EDGE,{"derivedFrom":sQuery(id+"F0.wireOp",EDGE,"E39")}),1.0]])]});
            var Q6;
            Q6=makeQuery(id+"F0.imprint","IMPRINT",FACE,{"disambiguationData":[TD([[makeQuery(id+"F0.imprint","IMPRINT",EDGE,{"derivedFrom":sQuery(id+"F0.wireOp",EDGE,"E40")}),1.0]])]});
            extrude(context, id + "F3", {"entities" : qUnion([Q0, Q1, Q2, Q3, Q4, Q5, Q6]), "depth" : 1 * mm, "hasSecondDirection" : true, "secondDirectionOppositeDirection" : true, "secondDirectionDepth" : -.8 * mm});
        }
    });
